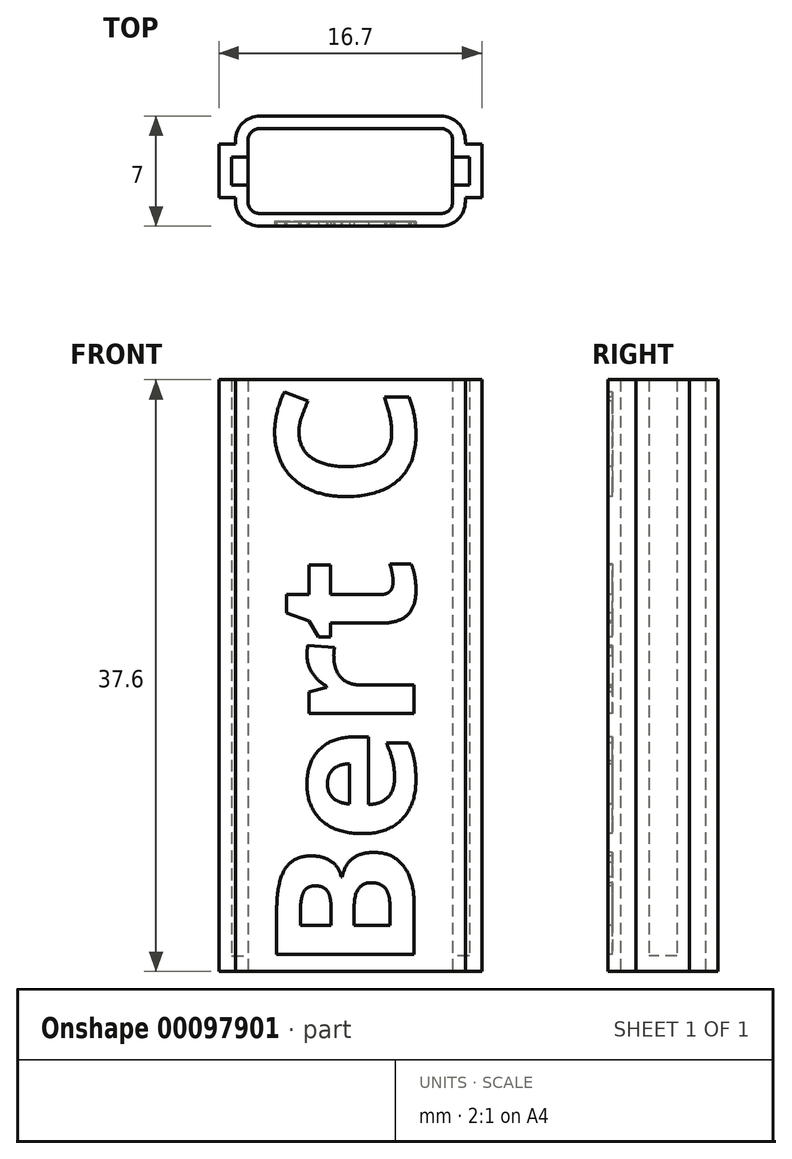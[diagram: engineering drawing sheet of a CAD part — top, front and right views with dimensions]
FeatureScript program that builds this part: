
annotation { "Feature Type Name" : "Feature", "Feature Type Description" : "" }
export const myFeature = defineFeature(function(context is Context, id is Id, definition is map)
    precondition{}
    {
        {
            var Q0;
            Q0=qCreatedBy(makeId("Top.planeOp"),FACE);
            var sketch = newSketch(context, id + "F0", { "sketchPlane" : qUnion([Q0])});
            skLineSegment(sketch, "E0.bottom", {"start": v(-15.06, 9.83) * mm, "end": v(-3.56, 9.83) * mm});
            skLineSegment(sketch, "E0.top", {"start": v(-15.06, 5.43) * mm, "end": v(-3.56, 5.43) * mm});
            skLineSegment(sketch, "E0.left", {"start": v(-15.31, 9.58) * mm, "end": v(-15.31, 8.03) * mm});
            skLineSegment(sketch, "E0.right", {"start": v(-3.31, 9.58) * mm, "end": v(-3.31, 8.03) * mm});
            skPoint(sketch, "E1.visualSharp", {"position": v(-15.31, 9.83) * mm});
            skArc(sketch, "E1.filletArc", {"start": v(-15.06, 9.83) * mm, "mid": v(-15.24, 9.75) * mm, "end": v(-15.31, 9.58) * mm});
            skPoint(sketch, "E2.visualSharp", {"position": v(-15.31, 5.43) * mm});
            skArc(sketch, "E2.filletArc", {"start": v(-15.31, 5.68) * mm, "mid": v(-15.24, 5.5) * mm, "end": v(-15.06, 5.43) * mm});
            skPoint(sketch, "E3.visualSharp", {"position": v(-3.31, 9.83) * mm});
            skArc(sketch, "E3.filletArc", {"start": v(-3.31, 9.58) * mm, "mid": v(-3.38, 9.75) * mm, "end": v(-3.56, 9.83) * mm});
            skPoint(sketch, "E4.visualSharp", {"position": v(-3.31, 5.43) * mm});
            skArc(sketch, "E4.filletArc", {"start": v(-3.56, 5.43) * mm, "mid": v(-3.38, 5.5) * mm, "end": v(-3.31, 5.68) * mm});
            skPoint(sketch, "E5", {"position": v(-15.31, 7.63) * mm});
            skPoint(sketch, "E6", {"position": v(-3.31, 7.63) * mm});
            skLineSegment(sketch, "E7", {"start": v(-15.31, 7.63) * mm, "end": v(-16.36, 7.63) * mm});
            skLineSegment(sketch, "E8", {"start": v(-3.31, 7.63) * mm, "end": v(-2.26, 7.63) * mm});
            skLineSegment(sketch, "E9", {"start": v(-16.36, 7.63) * mm, "end": v(-16.36, 8.03) * mm});
            skLineSegment(sketch, "E10", {"start": v(-16.36, 8.03) * mm, "end": v(-15.31, 8.03) * mm});
            skLineSegment(sketch, "E11", {"start": v(-16.36, 7.63) * mm, "end": v(-16.36, 7.23) * mm});
            skLineSegment(sketch, "E12", {"start": v(-16.36, 7.23) * mm, "end": v(-15.31, 7.23) * mm});
            skLineSegment(sketch, "E13", {"start": v(-2.26, 7.63) * mm, "end": v(-2.26, 7.23) * mm});
            skLineSegment(sketch, "E14", {"start": v(-2.26, 7.23) * mm, "end": v(-3.31, 7.23) * mm});
            skLineSegment(sketch, "E15", {"start": v(-2.26, 7.63) * mm, "end": v(-2.26, 8.03) * mm});
            skLineSegment(sketch, "E16", {"start": v(-2.26, 8.03) * mm, "end": v(-3.31, 8.03) * mm});
            skPoint(sketch, "E17.end.orphan", {"position": v(-16.36, 9.83) * mm});
            skPoint(sketch, "E18.orphan", {"position": v(-16.36, 5.43) * mm});
            skPoint(sketch, "E19.end.orphan", {"position": v(-2.26, 9.83) * mm});
            skPoint(sketch, "E20.orphan", {"position": v(-2.26, 5.43) * mm});
            skLineSegment(sketch, "E21", {"start": v(-15.31, 8.03) * mm, "end": v(-15.31, 7.23) * mm});
            skLineSegment(sketch, "E22", {"start": v(-15.31, 7.23) * mm, "end": v(-15.31, 5.68) * mm});
            skLineSegment(sketch, "E23", {"start": v(-3.31, 7.23) * mm, "end": v(-3.31, 5.68) * mm});
            skLineSegment(sketch, "E24", {"start": v(-3.31, 8.03) * mm, "end": v(-3.31, 7.23) * mm});
            skArc(sketch, "E25.0", {"start": v(-15.06, 10.33) * mm, "mid": v(-15.6, 10.1) * mm, "end": v(-15.81, 9.58) * mm});
            skLineSegment(sketch, "E25.1", {"start": v(-15.06, 10.33) * mm, "end": v(-3.56, 10.33) * mm});
            skArc(sketch, "E25.2", {"start": v(-2.81, 9.58) * mm, "mid": v(-3.03, 10.1) * mm, "end": v(-3.56, 10.33) * mm});
            skLineSegment(sketch, "E25.3", {"start": v(-2.81, 9.58) * mm, "end": v(-2.81, 8.53) * mm});
            skLineSegment(sketch, "E25.4", {"start": v(-1.76, 8.53) * mm, "end": v(-2.81, 8.53) * mm});
            skLineSegment(sketch, "E25.5", {"start": v(-15.81, 9.58) * mm, "end": v(-15.81, 8.53) * mm});
            skLineSegment(sketch, "E25.6", {"start": v(-1.76, 7.63) * mm, "end": v(-1.76, 8.53) * mm});
            skLineSegment(sketch, "E25.7", {"start": v(-1.76, 7.63) * mm, "end": v(-1.76, 6.73) * mm});
            skLineSegment(sketch, "E25.8", {"start": v(-16.86, 6.73) * mm, "end": v(-15.81, 6.73) * mm});
            skLineSegment(sketch, "E25.9", {"start": v(-16.86, 7.63) * mm, "end": v(-16.86, 6.73) * mm});
            skLineSegment(sketch, "E25.10", {"start": v(-16.86, 7.63) * mm, "end": v(-16.86, 8.53) * mm});
            skLineSegment(sketch, "E25.11", {"start": v(-16.86, 8.53) * mm, "end": v(-15.81, 8.53) * mm});
            skLineSegment(sketch, "E25.12", {"start": v(-15.81, 6.73) * mm, "end": v(-15.81, 5.68) * mm});
            skArc(sketch, "E25.13", {"start": v(-15.81, 5.68) * mm, "mid": v(-15.6, 5.15) * mm, "end": v(-15.06, 4.93) * mm});
            skLineSegment(sketch, "E25.14", {"start": v(-15.06, 4.93) * mm, "end": v(-3.56, 4.93) * mm});
            skArc(sketch, "E25.15", {"start": v(-3.56, 4.93) * mm, "mid": v(-3.03, 5.15) * mm, "end": v(-2.81, 5.68) * mm});
            skLineSegment(sketch, "E25.16", {"start": v(-2.81, 6.73) * mm, "end": v(-2.81, 5.68) * mm});
            skLineSegment(sketch, "E25.17", {"start": v(-1.76, 6.73) * mm, "end": v(-2.81, 6.73) * mm});
            skArc(sketch, "E26.0", {"start": v(-15.06, 11.13) * mm, "mid": v(-16.16, 10.67) * mm, "end": v(-16.61, 9.58) * mm});
            skLineSegment(sketch, "E26.1", {"start": v(-15.06, 11.13) * mm, "end": v(-3.56, 11.13) * mm});
            skArc(sketch, "E26.2", {"start": v(-2.01, 9.58) * mm, "mid": v(-2.46, 10.67) * mm, "end": v(-3.56, 11.13) * mm});
            skLineSegment(sketch, "E26.3", {"start": v(-2.01, 9.58) * mm, "end": v(-2.01, 9.33) * mm});
            skLineSegment(sketch, "E26.4", {"start": v(-0.96, 9.33) * mm, "end": v(-2.01, 9.33) * mm});
            skLineSegment(sketch, "E26.5", {"start": v(-16.61, 9.58) * mm, "end": v(-16.61, 9.33) * mm});
            skLineSegment(sketch, "E26.6", {"start": v(-0.96, 7.63) * mm, "end": v(-0.96, 9.33) * mm});
            skLineSegment(sketch, "E26.7", {"start": v(-0.96, 7.63) * mm, "end": v(-0.96, 5.93) * mm});
            skLineSegment(sketch, "E26.8", {"start": v(-17.66, 5.93) * mm, "end": v(-16.61, 5.93) * mm});
            skLineSegment(sketch, "E26.9", {"start": v(-17.66, 7.63) * mm, "end": v(-17.66, 5.93) * mm});
            skLineSegment(sketch, "E26.10", {"start": v(-17.66, 7.63) * mm, "end": v(-17.66, 9.33) * mm});
            skLineSegment(sketch, "E26.11", {"start": v(-17.66, 9.33) * mm, "end": v(-16.61, 9.33) * mm});
            skLineSegment(sketch, "E26.12", {"start": v(-16.61, 5.93) * mm, "end": v(-16.61, 5.68) * mm});
            skArc(sketch, "E26.13", {"start": v(-16.61, 5.68) * mm, "mid": v(-16.16, 4.58) * mm, "end": v(-15.06, 4.13) * mm});
            skLineSegment(sketch, "E26.14", {"start": v(-15.06, 4.13) * mm, "end": v(-3.56, 4.13) * mm});
            skArc(sketch, "E26.15", {"start": v(-3.56, 4.13) * mm, "mid": v(-2.46, 4.58) * mm, "end": v(-2.01, 5.68) * mm});
            skLineSegment(sketch, "E26.16", {"start": v(-2.01, 5.93) * mm, "end": v(-2.01, 5.68) * mm});
            skLineSegment(sketch, "E26.17", {"start": v(-0.96, 5.93) * mm, "end": v(-2.01, 5.93) * mm});
            skLineSegment(sketch, "E27", {"start": v(-15.81, 8.53) * mm, "end": v(-15.81, 6.73) * mm});
            skLineSegment(sketch, "E28", {"start": v(-2.81, 8.53) * mm, "end": v(-2.81, 6.73) * mm});
            skSolve(sketch);
        }
        {
            var Q0;
            Q0=makeQuery(id+"F0.imprint","IMPRINT",FACE,{"disambiguationData":[TD([[makeQuery(id+"F0.imprint","IMPRINT",EDGE,{"derivedFrom":sQuery(id+"F0.wireOp",EDGE,"E25.0")}),-1.0]])]});
            extrude(context, id + "F1", {"entities" : qUnion([Q0]), "depth" : 36.6 * mm});
        }
        {
            var Q0;
            Q0=makeQuery(id+"F0.imprint","IMPRINT",FACE,{"disambiguationData":[TD([[makeQuery(id+"F0.imprint","IMPRINT",EDGE,{"derivedFrom":sQuery(id+"F0.wireOp",EDGE,"E25.0")}),-1.0]])]});
            var Q1;
            {var subQ4=sQuery(id+"F0.wireOp",EDGE,"E9");Q1=makeQuery(id+"F0.imprint","IMPRINT",FACE,{"disambiguationData":[TD([[makeQuery(id+"F0.imprint","IMPRINT",EDGE,{"derivedFrom":subQ4}),1.0]])]});}
            var Q2;
            {var subQ0=sQuery(id+"F0.wireOp",EDGE,"E9");Q2=makeQuery(id+"F0.imprint","IMPRINT",FACE,{"disambiguationData":[TD([[makeQuery(id+"F0.imprint","IMPRINT",EDGE,{"derivedFrom":subQ0}),-1.0]])]});}
            var Q3;
            {var subQ0=sQuery(id+"F0.wireOp",EDGE,"E11");Q3=makeQuery(id+"F0.imprint","IMPRINT",FACE,{"disambiguationData":[TD([[makeQuery(id+"F0.imprint","IMPRINT",EDGE,{"derivedFrom":subQ0}),1.0]])]});}
            var Q4;
            {var subQ0=sQuery(id+"F0.wireOp",EDGE,"E15");Q4=makeQuery(id+"F0.imprint","IMPRINT",FACE,{"disambiguationData":[TD([[makeQuery(id+"F0.imprint","IMPRINT",EDGE,{"derivedFrom":subQ0}),1.0]])]});}
            var Q5;
            {var subQ0=sQuery(id+"F0.wireOp",EDGE,"E13");Q5=makeQuery(id+"F0.imprint","IMPRINT",FACE,{"disambiguationData":[TD([[makeQuery(id+"F0.imprint","IMPRINT",EDGE,{"derivedFrom":subQ0}),-1.0]])]});}
            var Q6;
            {var subQ6=sQuery(id+"F0.wireOp",EDGE,"E13");Q6=makeQuery(id+"F0.imprint","IMPRINT",FACE,{"disambiguationData":[TD([[makeQuery(id+"F0.imprint","IMPRINT",EDGE,{"derivedFrom":subQ6}),1.0]])]});}
            extrude(context, id + "F2", {"entities" : qUnion([Q0, Q1, Q2, Q3, Q4, Q5, Q6]), "operationType" : NewBodyOperationType.ADD, "oppositeDirection" : true, "depth" : 1 * mm});
        }
        {
            var Q0;
            {var subQ0=sQuery(id+"F0.wireOp",EDGE,"E26.14");Q0=makeQuery(id+"F2.boolean.opBoolean","MERGE",FACE,{"derivedFrom":[makeQuery(id+"F1.opExtrude","SWEPT_FACE",FACE,{"disambiguationData":[OSD([subQ0])]}),makeQuery(id+"F2.opExtrude","SWEPT_FACE",FACE,{"disambiguationData":[OSD([subQ0])]})]});}
            var sketch = newSketch(context, id + "F3", { "sketchPlane" : qUnion([Q0])});
            skLineSegment(sketch, "E29.0", {"start": v(-15.06, 36.6) * mm, "end": v(-15.06, -1) * mm});
            skLineSegment(sketch, "E29.1", {"start": v(-15.06, 36.6) * mm, "end": v(-3.56, 36.6) * mm});
            skLineSegment(sketch, "E29.2", {"start": v(-3.56, 36.6) * mm, "end": v(-3.56, -1) * mm});
            skLineSegment(sketch, "E29.3", {"start": v(-15.06, -1) * mm, "end": v(-3.56, -1) * mm});
            skText(sketch, "E30", { "text": "Bert C", "fontName": "OpenSans-Bold.ttf"});
            const initialGuessF3  = {"E30": [-0.00527, -0.001, 0, 1, 0.0088]};
            skSetInitialGuess(sketch, initialGuessF3);
            skSolve(sketch);
        }
        {
            var Q0;
            Q0=makeQuery(id+"F3.imprint","IMPRINT",FACE,{"disambiguationData":[TD([[makeQuery(id+"F3.imprint","IMPRINT",EDGE,{"derivedFrom":sQuery(id+"F3.wireOp",EDGE,"E30.sketch_text.stroke-76")}),-1.0]])]});
            var Q1;
            Q1=makeQuery(id+"F3.imprint","IMPRINT",FACE,{"disambiguationData":[TD([[makeQuery(id+"F3.imprint","IMPRINT",EDGE,{"derivedFrom":sQuery(id+"F3.wireOp",EDGE,"E30.sketch_text.stroke-58")}),-1.0]])]});
            var Q2;
            Q2=makeQuery(id+"F3.imprint","IMPRINT",FACE,{"disambiguationData":[TD([[makeQuery(id+"F3.imprint","IMPRINT",EDGE,{"derivedFrom":sQuery(id+"F3.wireOp",EDGE,"E30.sketch_text.stroke-45")}),-1.0]])]});
            var Q3;
            Q3=makeQuery(id+"F3.imprint","IMPRINT",FACE,{"disambiguationData":[TD([[makeQuery(id+"F3.imprint","IMPRINT",EDGE,{"derivedFrom":sQuery(id+"F3.wireOp",EDGE,"E30.sketch_text.stroke-25")}),-1.0]])]});
            var Q4;
            Q4=makeQuery(id+"F3.imprint","IMPRINT",FACE,{"disambiguationData":[TD([[makeQuery(id+"F3.imprint","IMPRINT",EDGE,{"derivedFrom":sQuery(id+"F3.wireOp",EDGE,"E30.sketch_text.stroke-0")}),-1.0]])]});
            extrude(context, id + "F4", {"entities" : qUnion([Q0, Q1, Q2, Q3, Q4]), "operationType" : NewBodyOperationType.REMOVE, "oppositeDirection" : true, "depth" : .3 * mm});
        }
    });
